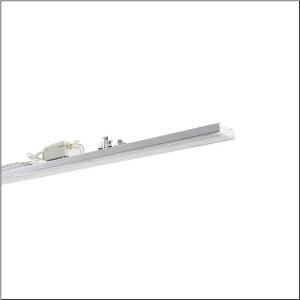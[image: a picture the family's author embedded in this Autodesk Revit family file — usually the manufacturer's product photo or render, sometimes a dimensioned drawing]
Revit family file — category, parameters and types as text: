
# Revit family: licross_r__21_recessed_mo_52te12dv4fxg3c_16ce
name_source: partatom
category: Lighting Fixtures
units: mm (PartAtom-declared; Revit-internal decimal feet)

## family parameters
Cut with Voids When Loaded = No
Host = Face
Light Source = No
Part Type = Normal
Room Calculation Point = No
Round Connector Dimension = Use Diameter
Shared = No

## types (1)
- --- (1 x LED, 950 lm, 5.5 W, 4000K)
    Apparent Load = 6 VA
    CIE Flux Codes = 72 92 99 100 100
    Color Rendering = 80
    Color Temperature = 4000K
    Default Elevation = 1800 mm
    Description = Licross® 21 Recessed MO, luminaire insert, of sheet steel, galvanised, coil coated, white, length: 2.250mm, width: 66mm, height: 67mm, LED rated luminous flux: 15.420lm, light colour: 840, control gear: DALI 2, with plug, 6-pole, with phase selection, for trunking rail, 14-core, mains connection: 220..240V, AC, 50/60Hz, rated input power: 89W, for trunking rail, 14-core, halogen-free wiring, for emergency light function, converter,control gear: single battery element, battery: LiFeP04, 9Ah, primary optical cover: cover, of PMMA, light emission: direct distribution, primary light characteristic: symmetric, protection rating (complete): IP54, insulation class (complete): insulation class I (protective earthing), certification: CE, UKCA, protection symbol: D if used in an environment with non-conductive dust loads with corresponding accessories, impact resistance: IK06, permissible ambient temperature for indoor applications: +5..+35°C, standard: EN 60598-2-22, LABS conformity tested according to VDMA 24364:2018-05, reducing of maximum allowable ambient temperature of 5°C with ceiling mounting, corresponds to IFS (International Featured Standards) requirements for safety and quality in the food industry, packaging unit: 1 piece
    Height = 58 mm
    Lamp = 1 x LED
    Lamp Light Flux = 950 lm
    Lamp Power = 5.5 W
    Lamp count = 1
    Length = 2250 mm
    Luminous efficacy = 173 lm/W
    Manufacturer = Siteco
    ModVariant = No
    Model = 52TE12DV4FXG3C
    Mounting Place = Ceiling
    Mounting Type = Pendant
    Number of Poles = 1
    OnlyDefault = Yes
    Power Factor = 1
    Product Name = Licross® 21 Recessed MO
    Product group = luminaire insert
    ProductGroupID = 901
    Protection Class = Protection class I
    Protection Degree = IP 54
    RLX_Detail_Level = 1
    RLX_Emergency_Light_Flux = 0 lm
    RLX_Emergency_Type = 0
    RLX_Emergency_Type_DB = No
    RlxData = <blob elided: 30105 chars, md5=1212be87>
    Socket = socket
    Standby Power = 0 W
    System Light Flux = 950 lm
    System Power = 6 W
    Type Comments = : emergency light operation: 3 h
    Type Image = l_1296930.jpg
    URL = http://relux.com
    VarID = @adj_040193
    Voltage = 0 V
    Weight = 0.00 kg
    Width = 66 mm

## geometry (parser evidence)
native form markers: Blend x4, Sweep x10
no freeform markers — native parametric forms only
